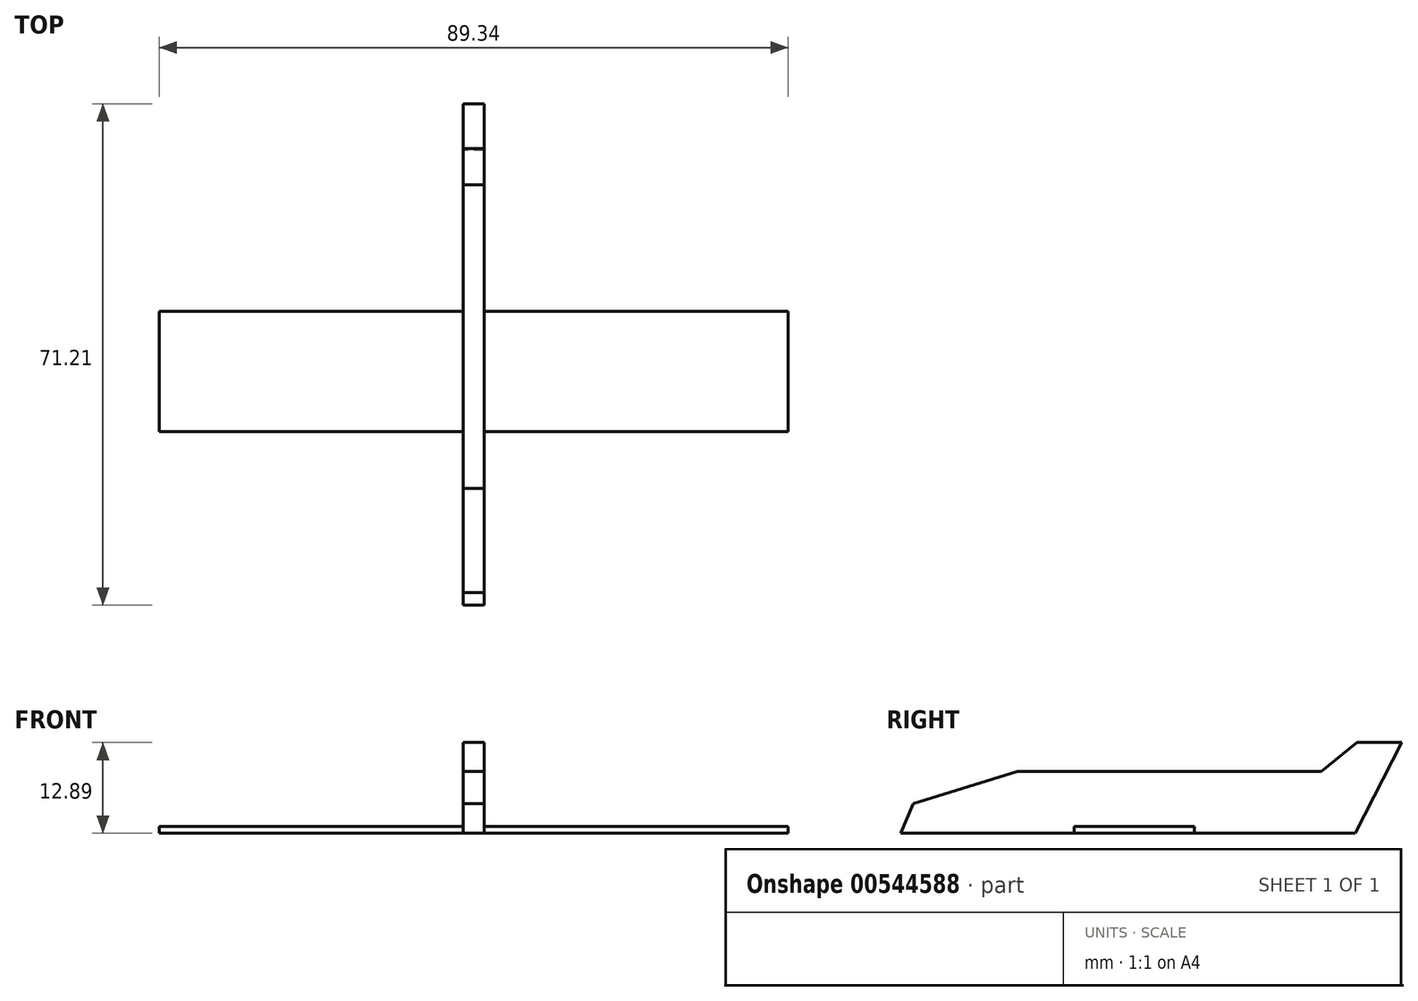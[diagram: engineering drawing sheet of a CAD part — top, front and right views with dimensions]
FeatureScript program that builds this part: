
annotation { "Feature Type Name" : "Feature", "Feature Type Description" : "" }
export const myFeature = defineFeature(function(context is Context, id is Id, definition is map)
    precondition{}
    {
        {
            var Q0;
            Q0=qCreatedBy(makeId("Right.planeOp"),FACE);
            var sketch = newSketch(context, id + "F0", { "sketchPlane" : qUnion([Q0])});
            skLineSegment(sketch, "E0", {"start": v(-33.18, 0) * mm, "end": v(31.4, 0) * mm});
            skLineSegment(sketch, "E1", {"start": v(31.4, 0) * mm, "end": v(38.03, 12.9) * mm});
            skLineSegment(sketch, "E2", {"start": v(38.03, 12.9) * mm, "end": v(31.65, 12.9) * mm});
            skLineSegment(sketch, "E3", {"start": v(31.65, 12.9) * mm, "end": v(26.55, 8.8) * mm});
            skLineSegment(sketch, "E4", {"start": v(26.55, 8.8) * mm, "end": v(-16.6, 8.8) * mm});
            skLineSegment(sketch, "E5", {"start": v(-16.6, 8.8) * mm, "end": v(-31.4, 4.21) * mm});
            skLineSegment(sketch, "E6", {"start": v(-31.4, 4.21) * mm, "end": v(-33.18, 0) * mm});
            skSolve(sketch);
        }
        {
            var Q0;
            Q0 = qSketchRegion(id + "F0", true);
            extrude(context, id + "F1", {"entities" : qUnion([Q0]), "endBound" : BoundingType.SYMMETRIC, "depth" : 3 * mm, "offsetDistance" : 25 * mm});
        }
        {
            var Q0;
            Q0=qCreatedBy(makeId("Top.planeOp"),FACE);
            var sketch = newSketch(context, id + "F2", { "sketchPlane" : qUnion([Q0])});
            skLineSegment(sketch, "E7.bottom", {"start": v(44.67, -8.55) * mm, "end": v(-44.67, -8.55) * mm});
            skLineSegment(sketch, "E7.top", {"start": v(44.67, 8.55) * mm, "end": v(-44.67, 8.55) * mm});
            skLineSegment(sketch, "E7.left", {"start": v(44.67, -8.55) * mm, "end": v(44.67, 8.55) * mm});
            skLineSegment(sketch, "E7.right", {"start": v(-44.67, -8.55) * mm, "end": v(-44.67, 8.55) * mm});
            skPoint(sketch, "E7.middle", {"position": v(0, 0) * mm});
            skSolve(sketch);
        }
        {
            var Q0;
            Q0 = qSketchRegion(id + "F2", true);
            extrude(context, id + "F3", {"entities" : qUnion([Q0]), "operationType" : NewBodyOperationType.ADD, "depth" : 1 * mm, "offsetDistance" : 25 * mm});
        }
    });
